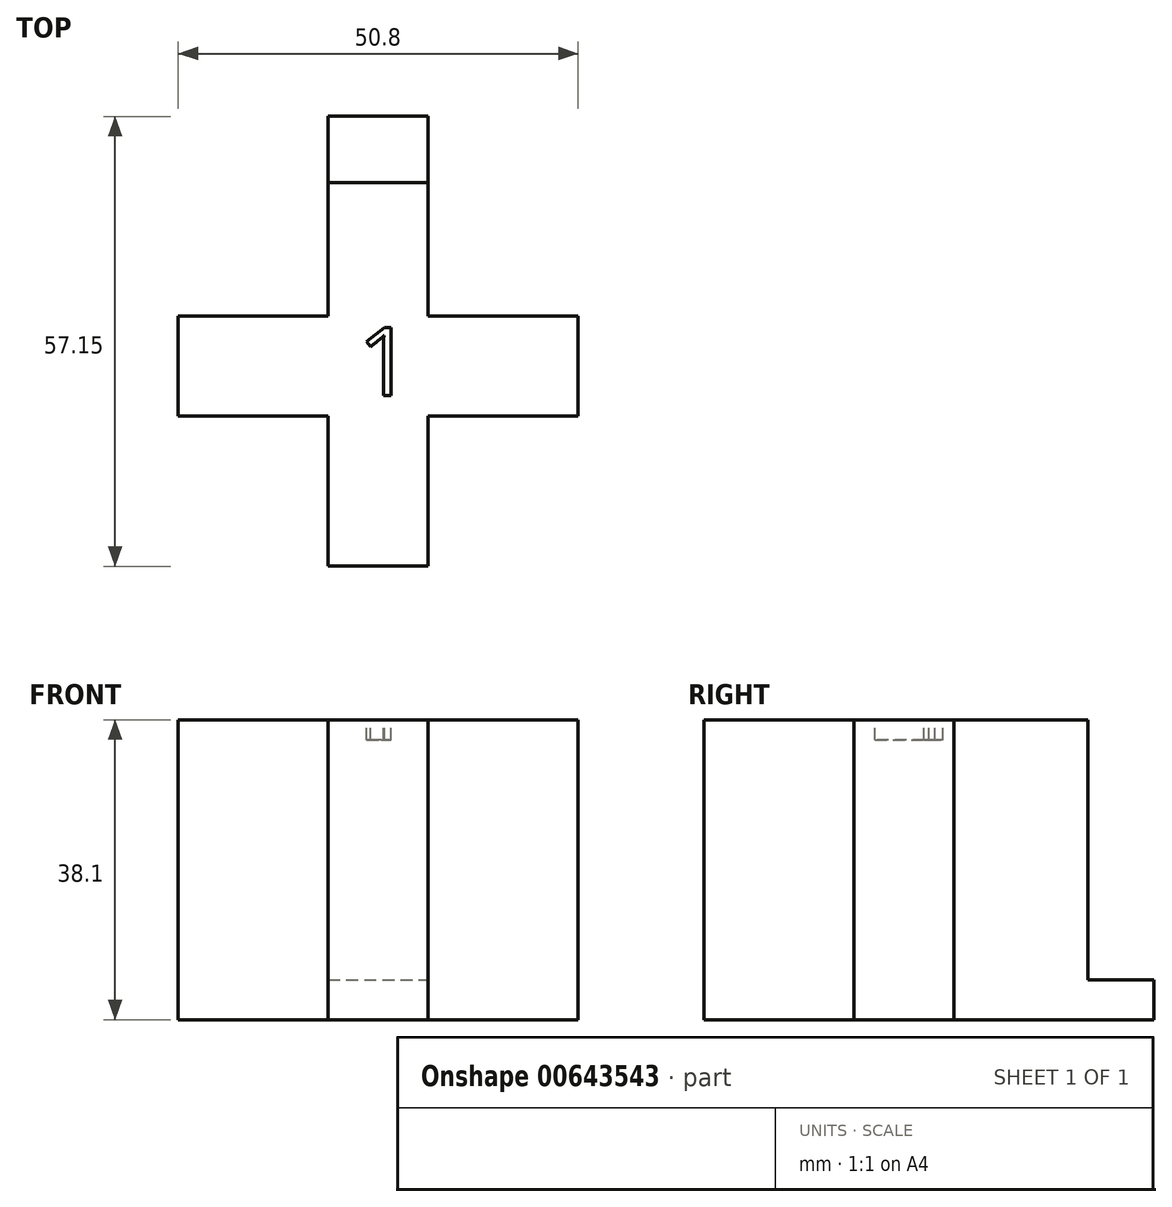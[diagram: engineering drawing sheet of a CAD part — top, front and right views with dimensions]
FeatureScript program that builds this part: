
annotation { "Feature Type Name" : "Feature", "Feature Type Description" : "" }
export const myFeature = defineFeature(function(context is Context, id is Id, definition is map)
    precondition{}
    {
        {
            var Q0;
            Q0=qCreatedBy(makeId("Top.planeOp"),FACE);
            var sketch = newSketch(context, id + "F0", { "sketchPlane" : qUnion([Q0])});
            skLineSegment(sketch, "E0.bottom", {"start": v(-43.37, 31.57) * mm, "end": v(-30.67, 31.57) * mm});
            skLineSegment(sketch, "E0.top", {"start": v(-43.37, -25.58) * mm, "end": v(-30.67, -25.58) * mm});
            skLineSegment(sketch, "E0.left", {"start": v(-43.37, 31.57) * mm, "end": v(-43.37, -25.58) * mm});
            skLineSegment(sketch, "E0.right", {"start": v(-30.67, 31.57) * mm, "end": v(-30.67, -25.58) * mm});
            skSolve(sketch);
        }
        {
            var Q0;
            Q0 = qSketchRegion(id + "F0", true);
            extrude(context, id + "F1", {"entities" : qUnion([Q0]), "depth" : 5.08 * mm, "offsetDistance" : 25.4 * mm});
        }
        {
            var Q0;
            Q0=qCreatedBy(makeId("Top.planeOp"),FACE);
            var sketch = newSketch(context, id + "F2", { "sketchPlane" : qUnion([Q0])});
            skLineSegment(sketch, "E1.bottom", {"start": v(-62.42, -6.53) * mm, "end": v(-11.62, -6.53) * mm});
            skLineSegment(sketch, "E1.top", {"start": v(-62.42, 6.17) * mm, "end": v(-11.62, 6.17) * mm});
            skLineSegment(sketch, "E1.left", {"start": v(-62.42, -6.53) * mm, "end": v(-62.42, 6.17) * mm});
            skLineSegment(sketch, "E1.right", {"start": v(-11.62, -6.53) * mm, "end": v(-11.62, 6.17) * mm});
            skSolve(sketch);
        }
        {
            var Q0;
            Q0 = qSketchRegion(id + "F2", true);
            extrude(context, id + "F3", {"entities" : qUnion([Q0]), "operationType" : NewBodyOperationType.ADD, "depth" : 38.1 * mm, "offsetDistance" : 25.4 * mm});
        }
        {
            var Q0;
            {var subQ0=sQuery(id+"F0.wireOp",EDGE,"E0.top");var subQ1=sQuery(id+"F0.wireOp",EDGE,"E0.left");var subQ2=sQuery(id+"F0.wireOp",EDGE,"E0.right");Q0=makeQuery(id+"F3.boolean.opBoolean","SPLIT",FACE,{"disambiguationData":[TD([makeQuery(id+"F1.opExtrude","SWEPT_FACE",FACE,{"disambiguationData":[OSD([subQ0])]})])],"derivedFrom":makeQuery(id+"F1.opExtrude","CAP_FACE",FACE,{"disambiguationData":[OSD([sQuery(id+"F0.wireOp",EDGE,"E0.bottom"),subQ0,subQ1,subQ2])],"isStart":false})});}
            var sketch = newSketch(context, id + "F4", { "sketchPlane" : qUnion([Q0])});
            skLineSegment(sketch, "E2.bottom", {"start": v(-30.67, -25.58) * mm, "end": v(-43.37, -25.58) * mm});
            skLineSegment(sketch, "E2.top", {"start": v(-30.67, 23.16) * mm, "end": v(-43.37, 23.16) * mm});
            skLineSegment(sketch, "E2.left", {"start": v(-30.67, -25.58) * mm, "end": v(-30.67, 23.16) * mm});
            skLineSegment(sketch, "E2.right", {"start": v(-43.37, -25.58) * mm, "end": v(-43.37, 23.16) * mm});
            skSolve(sketch);
        }
        {
            var Q0;
            Q0 = qSketchRegion(id + "F4", true);
            extrude(context, id + "F5", {"entities" : qUnion([Q0]), "operationType" : NewBodyOperationType.ADD, "depth" : 33.02 * mm, "offsetDistance" : 25.4 * mm});
        }
        {
            var Q0;
            Q0=makeQuery(id+"F5.boolean.opBoolean","MERGE",FACE,{"derivedFrom":[makeQuery(id+"F3.opExtrude","CAP_FACE",FACE,{"disambiguationData":[OSD([sQuery(id+"F2.wireOp",EDGE,"E1.bottom"),sQuery(id+"F2.wireOp",EDGE,"E1.top"),sQuery(id+"F2.wireOp",EDGE,"E1.left"),sQuery(id+"F2.wireOp",EDGE,"E1.right")])],"isStart":false}),makeQuery(id+"F5.opExtrude","CAP_FACE",FACE,{"disambiguationData":[OSD([sQuery(id+"F4.wireOp",EDGE,"E2.bottom"),sQuery(id+"F4.wireOp",EDGE,"E2.top"),sQuery(id+"F4.wireOp",EDGE,"E2.left"),sQuery(id+"F4.wireOp",EDGE,"E2.right")])],"isStart":false})]});
            var sketch = newSketch(context, id + "F6", { "sketchPlane" : qUnion([Q0])});
            skText(sketch, "E3", { "text": "1", "fontName": "OpenSans-Regular.ttf"});
            const initialGuessF6  = {"E3": [-0.0396, -0.00387, 1, 0, 0.0087]};
            skSetInitialGuess(sketch, initialGuessF6);
            skSolve(sketch);
        }
        {
            var Q0;
            Q0 = qSketchRegion(id + "F6", true);
            extrude(context, id + "F7", {"entities" : qUnion([Q0]), "operationType" : NewBodyOperationType.REMOVE, "oppositeDirection" : true, "depth" : 2.54 * mm, "offsetDistance" : 25.4 * mm});
        }
    });
